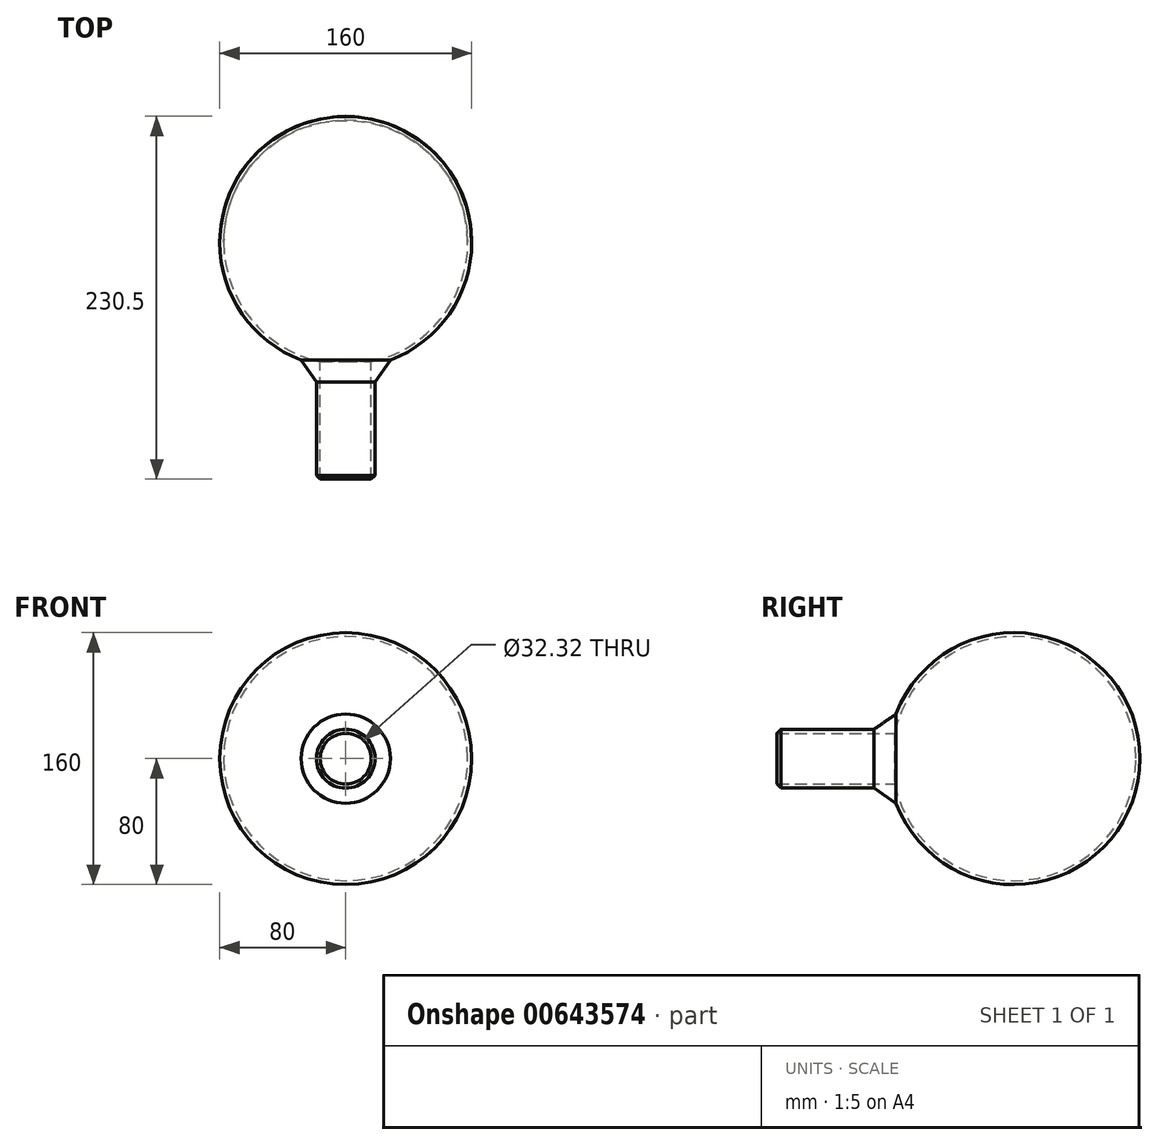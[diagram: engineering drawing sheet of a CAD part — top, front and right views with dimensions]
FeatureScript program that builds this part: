
annotation { "Feature Type Name" : "Feature", "Feature Type Description" : "" }
export const myFeature = defineFeature(function(context is Context, id is Id, definition is map)
    precondition{}
    {
        {
            var Q0;
            Q0=qCreatedBy(makeId("Top.planeOp"),FACE);
            var sketch = newSketch(context, id + "F0", { "sketchPlane" : qUnion([Q0])});
            skCircle(sketch, "E0", {"center": v(0, 0) * mm, "radius": 80 * mm});
            skLineSegment(sketch, "E1", {"start": v(80, 0) * mm, "end": v(-80, 0) * mm});
            skSolve(sketch);
        }
        {
            var Q0;
            {var subQ0=sQuery(id+"F0.wireOp",EDGE,"E1");Q0=makeQuery(id+"F0.imprint","IMPRINT",FACE,{"disambiguationData":[TD([[makeQuery(id+"F0.imprint","IMPRINT",EDGE,{"derivedFrom":subQ0}),-1.0]])]});}
            var Q1;
            Q1=sQuery(id+"F0.wireOp",EDGE,"E1");
            revolve(context, id + "F1", {"entities" : qUnion([Q0]), "axis" : qUnion([Q1]), "revolveType" : RevolveType.FULL});
        }
        {
            var Q0;
            Q0=qCreatedBy(makeId("Front.planeOp"),FACE);
            var sketch = newSketch(context, id + "F2", { "sketchPlane" : qUnion([Q0])});
            skCircle(sketch, "E2", {"center": v(0, 0) * mm, "radius": 18.66 * mm});
            skSolve(sketch);
        }
        {
            var Q0;
            Q0 = qSketchRegion(id + "F2", true);
            extrude(context, id + "F3", {"entities" : qUnion([Q0]), "operationType" : NewBodyOperationType.ADD, "depth" : 163 * mm, "offsetDistance" : 25 * mm});
        }
        {
            var Q0;
            Q0=makeQuery(id+"F3.opExtrude","CAP_FACE",FACE,{"disambiguationData":[OSD([sQuery(id+"F2.wireOp",EDGE,"E2")])],"isStart":false});
            shell(context, id + "F4", {"entities" : qUnion([Q0]), "thickness" : 2.5 * mm});
        }
        {
            var Q0;
            Q0=makeQuery(id+"F3.opExtrude","SWEPT_FACE",FACE,{"disambiguationData":[OSD([sQuery(id+"F2.wireOp",EDGE,"E2")])]});
            chamfer(context, id + "F5", {"entities" : qUnion([Q0]), "width" : 15 * mm, "tangentPropagation" : true});
        }
    });
